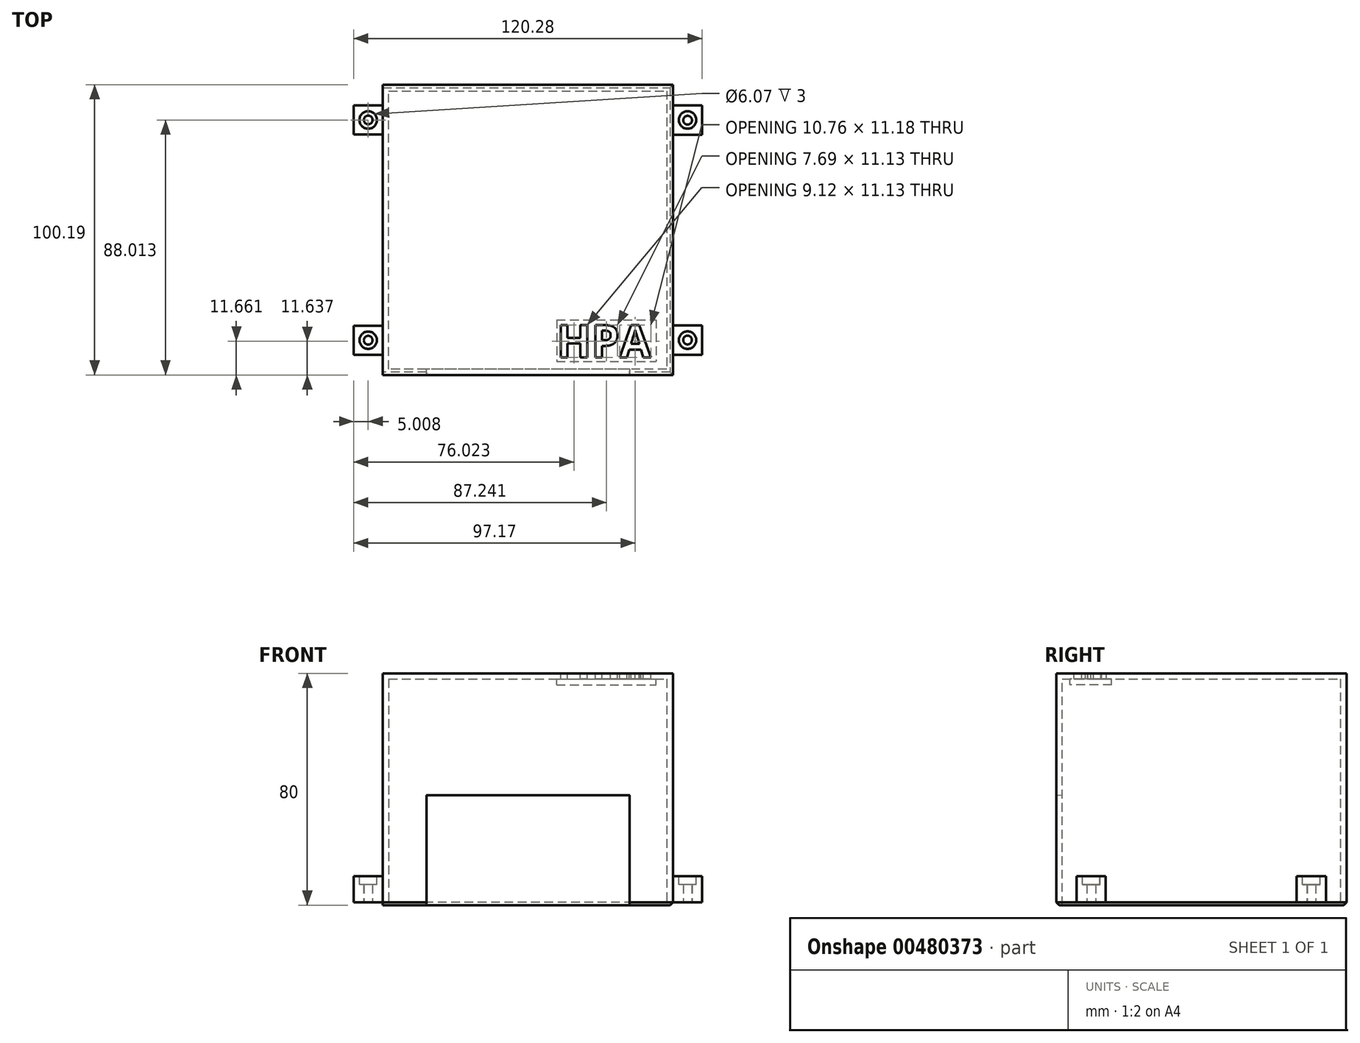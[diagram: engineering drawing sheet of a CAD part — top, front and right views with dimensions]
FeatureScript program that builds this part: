
annotation { "Feature Type Name" : "Feature", "Feature Type Description" : "" }
export const myFeature = defineFeature(function(context is Context, id is Id, definition is map)
    precondition{}
    {
        {
            var Q0;
            Q0=qCreatedBy(makeId("Right.planeOp"),FACE);
            cPlane(context, id + "F0", {"entities" : qUnion([Q0]), "cplaneType" : CPlaneType.OFFSET, "offset" : 100 * mm, "width" : 150 * mm, "height" : 150 * mm});
        }
        {
            var Q0;
            Q0=qCreatedBy(makeId("Front.planeOp"),FACE);
            cPlane(context, id + "F1", {"entities" : qUnion([Q0]), "cplaneType" : CPlaneType.OFFSET, "offset" : 100 * mm, "oppositeDirection" : true, "width" : 150 * mm, "height" : 150 * mm});
        }
        {
            var Q0;
            Q0=qCreatedBy(makeId("Top.planeOp"),FACE);
            var sketch = newSketch(context, id + "F2", { "sketchPlane" : qUnion([Q0])});
            skLineSegment(sketch, "E0.bottom", {"start": v(0, 0) * mm, "end": v(100.19, 0) * mm});
            skLineSegment(sketch, "E0.top", {"start": v(0, 100.19) * mm, "end": v(100.19, 100.19) * mm});
            skLineSegment(sketch, "E0.left", {"start": v(0, 0) * mm, "end": v(0, 100.19) * mm});
            skLineSegment(sketch, "E0.right", {"start": v(100.19, 0) * mm, "end": v(100.19, 100.19) * mm});
            skSolve(sketch);
        }
        {
            var Q0;
            Q0=qCreatedBy(id+"F1.planeOp",FACE);
            cPlane(context, id + "F3", {"entities" : qUnion([Q0]), "cplaneType" : CPlaneType.OFFSET, "offset" : 2 * mm, "width" : 150 * mm, "height" : 150 * mm});
        }
        {
            var Q0;
            Q0=qCreatedBy(makeId("Front.planeOp"),FACE);
            cPlane(context, id + "F4", {"entities" : qUnion([Q0]), "cplaneType" : CPlaneType.OFFSET, "offset" : 2 * mm, "oppositeDirection" : true, "width" : 150 * mm, "height" : 150 * mm});
        }
        {
            var Q0;
            Q0=qCreatedBy(makeId("Top.planeOp"),FACE);
            var sketch = newSketch(context, id + "F5", { "sketchPlane" : qUnion([Q0])});
            skLineSegment(sketch, "E1.bottom", {"start": v(2, 2) * mm, "end": v(97.96, 2) * mm});
            skLineSegment(sketch, "E1.top", {"start": v(2, 98.03) * mm, "end": v(97.96, 98.03) * mm});
            skLineSegment(sketch, "E1.left", {"start": v(2, 2) * mm, "end": v(2, 98.03) * mm});
            skLineSegment(sketch, "E1.right", {"start": v(97.96, 2) * mm, "end": v(97.96, 98.03) * mm});
            skSolve(sketch);
        }
        {
            var Q0;
            Q0=makeQuery(id+"F2.imprint","IMPRINT",FACE,{"disambiguationData":[TD([[makeQuery(id+"F2.imprint","IMPRINT",EDGE,{"derivedFrom":sQuery(id+"F2.wireOp",EDGE,"E0.bottom")}),1.0]])]});
            extrude(context, id + "F6", {"entities" : qUnion([Q0]), "depth" : 80 * mm, "hasDraft" : true, "draftAngle" : 0 * degree});
        }
        {
            var Q0;
            Q0 = qSketchRegion(id + "F5", true);
            extrude(context, id + "F7", {"entities" : qUnion([Q0]), "operationType" : NewBodyOperationType.REMOVE, "depth" : 78 * mm, "hasDraft" : true, "draftAngle" : 0 * degree});
        }
        {
            var Q0;
            Q0=qCreatedBy(makeId("Top.planeOp"),FACE);
            var sketch = newSketch(context, id + "F8", { "sketchPlane" : qUnion([Q0])});
            skLineSegment(sketch, "E2.bottom", {"start": v(0, 93.06) * mm, "end": v(-10.06, 93.06) * mm});
            skLineSegment(sketch, "E2.top", {"start": v(0, 82.97) * mm, "end": v(-10.06, 82.97) * mm});
            skLineSegment(sketch, "E2.left", {"start": v(0, 93.06) * mm, "end": v(0, 82.97) * mm});
            skLineSegment(sketch, "E2.right", {"start": v(-10.06, 93.06) * mm, "end": v(-10.06, 82.97) * mm});
            skSolve(sketch);
        }
        {
            var Q0;
            Q0=qCreatedBy(makeId("Top.planeOp"),FACE);
            var sketch = newSketch(context, id + "F9", { "sketchPlane" : qUnion([Q0])});
            skLineSegment(sketch, "E3.bottom", {"start": v(0, 6.97) * mm, "end": v(-10.04, 6.97) * mm});
            skLineSegment(sketch, "E3.top", {"start": v(0, 17.01) * mm, "end": v(-10.04, 17.01) * mm});
            skLineSegment(sketch, "E3.left", {"start": v(0, 6.97) * mm, "end": v(0, 17.01) * mm});
            skLineSegment(sketch, "E3.right", {"start": v(-10.04, 6.97) * mm, "end": v(-10.04, 17.01) * mm});
            skSolve(sketch);
        }
        {
            var Q0;
            Q0=qCreatedBy(makeId("Top.planeOp"),FACE);
            var sketch = newSketch(context, id + "F10", { "sketchPlane" : qUnion([Q0])});
            skLineSegment(sketch, "E4.bottom", {"start": v(100.16, 7) * mm, "end": v(110.2, 7) * mm});
            skLineSegment(sketch, "E4.top", {"start": v(100.16, 17.04) * mm, "end": v(110.2, 17.04) * mm});
            skLineSegment(sketch, "E4.left", {"start": v(100.16, 7) * mm, "end": v(100.16, 17.04) * mm});
            skLineSegment(sketch, "E4.right", {"start": v(110.2, 7) * mm, "end": v(110.2, 17.04) * mm});
            skSolve(sketch);
        }
        {
            var Q0;
            Q0=qCreatedBy(makeId("Top.planeOp"),FACE);
            var sketch = newSketch(context, id + "F11", { "sketchPlane" : qUnion([Q0])});
            skLineSegment(sketch, "E5.bottom", {"start": v(100.18, 93) * mm, "end": v(110.22, 93) * mm});
            skLineSegment(sketch, "E5.top", {"start": v(100.18, 82.95) * mm, "end": v(110.22, 82.95) * mm});
            skLineSegment(sketch, "E5.left", {"start": v(100.18, 93) * mm, "end": v(100.18, 82.95) * mm});
            skLineSegment(sketch, "E5.right", {"start": v(110.22, 93) * mm, "end": v(110.22, 82.95) * mm});
            skSolve(sketch);
        }
        {
            var Q0;
            Q0=makeQuery(id+"F6.opExtrude","CAP_FACE",FACE,{"disambiguationData":[OSD([sQuery(id+"F2.wireOp",EDGE,"E0.bottom"),sQuery(id+"F2.wireOp",EDGE,"E0.top"),sQuery(id+"F2.wireOp",EDGE,"E0.left"),sQuery(id+"F2.wireOp",EDGE,"E0.right")])],"isStart":false});
            cPlane(context, id + "F12", {"entities" : qUnion([Q0]), "cplaneType" : CPlaneType.OFFSET, "offset" : 0 * mm, "oppositeDirection" : true, "width" : 150 * mm, "height" : 150 * mm});
        }
        {
            var Q0;
            Q0=makeQuery(id+"F8.imprint","IMPRINT",FACE,{"disambiguationData":[TD([[makeQuery(id+"F8.imprint","IMPRINT",EDGE,{"derivedFrom":sQuery(id+"F8.wireOp",EDGE,"E2.bottom")}),1.0]])]});
            var Q1;
            Q1=makeQuery(id+"F11.imprint","IMPRINT",FACE,{"disambiguationData":[TD([[makeQuery(id+"F11.imprint","IMPRINT",EDGE,{"derivedFrom":sQuery(id+"F11.wireOp",EDGE,"E5.bottom")}),-1.0]])]});
            var Q2;
            Q2=makeQuery(id+"F10.imprint","IMPRINT",FACE,{"disambiguationData":[TD([[makeQuery(id+"F10.imprint","IMPRINT",EDGE,{"derivedFrom":sQuery(id+"F10.wireOp",EDGE,"E4.bottom")}),1.0]])]});
            var Q3;
            Q3=makeQuery(id+"F9.imprint","IMPRINT",FACE,{"disambiguationData":[TD([[makeQuery(id+"F9.imprint","IMPRINT",EDGE,{"derivedFrom":sQuery(id+"F9.wireOp",EDGE,"E3.bottom")}),-1.0]])]});
            extrude(context, id + "F13", {"entities" : qUnion([Q0, Q1, Q2, Q3]), "operationType" : NewBodyOperationType.ADD, "depth" : 10 * mm, "hasDraft" : true, "draftAngle" : 0 * degree});
        }
        {
            var Q0;
            Q0 = qSketchRegion(id + "F8", true);
            var Q1;
            Q1 = qSketchRegion(id + "F9", true);
            var Q2;
            Q2 = qSketchRegion(id + "F11", true);
            var Q3;
            Q3 = qSketchRegion(id + "F10", true);
            extrude(context, id + "F14", {"entities" : qUnion([Q0, Q1, Q2, Q3]), "operationType" : NewBodyOperationType.REMOVE, "depth" : 1 * mm, "hasDraft" : true, "draftAngle" : 0 * degree});
        }
        {
            var Q0;
            Q0=qCreatedBy(makeId("Top.planeOp"),FACE);
            var sketch = newSketch(context, id + "F15", { "sketchPlane" : qUnion([Q0])});
            skCircle(sketch, "E6", {"center": v(-5.05, 12) * mm, "radius": 3 * mm});
            skCircle(sketch, "E7", {"center": v(-5.05, 88.01) * mm, "radius": 3.03 * mm});
            skCircle(sketch, "E8", {"center": v(105.2, 88.01) * mm, "radius": 3.02 * mm});
            skCircle(sketch, "E9", {"center": v(105.2, 12.02) * mm, "radius": 3 * mm});
            skSolve(sketch);
        }
        {
            var Q0;
            Q0 = qSketchRegion(id + "F15", true);
            extrude(context, id + "F16", {"entities" : qUnion([Q0]), "operationType" : NewBodyOperationType.REMOVE, "depth" : 25 * mm, "hasDraft" : true, "draftAngle" : 0 * degree});
        }
        {
            var Q0;
            Q0 = qSketchRegion(id + "F15", true);
            extrude(context, id + "F17", {"entities" : qUnion([Q0]), "operationType" : NewBodyOperationType.ADD, "depth" : 7 * mm, "hasDraft" : true, "draftAngle" : 0 * degree});
        }
        {
            var Q0;
            Q0 = qSketchRegion(id + "F15", true);
            extrude(context, id + "F18", {"entities" : qUnion([Q0]), "operationType" : NewBodyOperationType.REMOVE, "depth" : 1 * mm, "hasDraft" : true, "draftAngle" : 0 * degree});
        }
        {
            var Q0;
            Q0=qCreatedBy(makeId("Top.planeOp"),FACE);
            var sketch = newSketch(context, id + "F19", { "sketchPlane" : qUnion([Q0])});
            skCircle(sketch, "E10", {"center": v(-5.05, 12) * mm, "radius": 1.52 * mm});
            skCircle(sketch, "E11", {"center": v(105.17, 12.04) * mm, "radius": 1.5 * mm});
            skCircle(sketch, "E12", {"center": v(105.22, 87.94) * mm, "radius": 1.5 * mm});
            skCircle(sketch, "E13", {"center": v(-5.04, 88.03) * mm, "radius": 1.51 * mm});
            skSolve(sketch);
        }
        {
            var Q0;
            Q0 = qSketchRegion(id + "F19", true);
            extrude(context, id + "F20", {"entities" : qUnion([Q0]), "operationType" : NewBodyOperationType.REMOVE, "depth" : 25 * mm});
        }
        {
            var Q0;
            Q0=qCreatedBy(makeId("Front.planeOp"),FACE);
            var sketch = newSketch(context, id + "F21", { "sketchPlane" : qUnion([Q0])});
            skLineSegment(sketch, "E14.bottom", {"start": v(15.03, 37.98) * mm, "end": v(85.18, 37.98) * mm});
            skLineSegment(sketch, "E14.top", {"start": v(15.03, -2.64) * mm, "end": v(85.18, -2.64) * mm});
            skLineSegment(sketch, "E14.left", {"start": v(15.03, 37.98) * mm, "end": v(15.03, -2.64) * mm});
            skLineSegment(sketch, "E14.right", {"start": v(85.18, 37.98) * mm, "end": v(85.18, -2.64) * mm});
            skSolve(sketch);
        }
        {
            var Q0;
            Q0 = qSketchRegion(id + "F21", true);
            extrude(context, id + "F22", {"entities" : qUnion([Q0]), "operationType" : NewBodyOperationType.REMOVE, "depth" : 25 * mm, "hasSecondDirection" : true, "secondDirectionOppositeDirection" : true, "secondDirectionDepth" : 25 * mm, "hasSecondDirectionDraft" : true, "secondDirectionDraftAngle" : 3 * degree});
        }
        {
            var Q0;
            Q0=qCreatedBy(id+"F12.planeOp",FACE);
            var sketch = newSketch(context, id + "F23", { "sketchPlane" : qUnion([Q0])});
            skText(sketch, "E15", { "text": "HPA", "fontName": "OpenSans-Bold.ttf"});
            const initialGuessF23  = {"E15": [0.06, 0.00607, 1, 0, 0.01123]};
            skSetInitialGuess(sketch, initialGuessF23);
            skSolve(sketch);
        }
        {
            var Q0;
            Q0=makeQuery(id+"F6.opExtrude","CAP_EDGE",EDGE,{"disambiguationData":[OSD([sQuery(id+"F2.wireOp",EDGE,"E0.top")])],"isStart":true});
            var Q1;
            Q1=makeQuery(id+"F7.boolean.opBoolean","COPY",EDGE,{"derivedFrom":makeQuery(id+"F7.opExtrude","CAP_EDGE",EDGE,{"disambiguationData":[OSD([sQuery(id+"F5.wireOp",EDGE,"E1.top")])],"isStart":true})});
            var Q2;
            {var subQ0=sQuery(id+"F9.wireOp",EDGE,"E3.left");var subQ1=sQuery(id+"F8.wireOp",EDGE,"E2.left");var subQ2=sQuery(id+"F8.wireOp",EDGE,"E2.top");var subQ3=sQuery(id+"F2.wireOp",EDGE,"E0.left");var subQ7=sQuery(id+"F2.wireOp",EDGE,"E0.top");var subQ8=sQuery(id+"F2.wireOp",EDGE,"E0.bottom");var subQ15=makeQuery(id+"F6.opExtrude","CAP_EDGE",EDGE,{"disambiguationData":[OSD([subQ3])],"isStart":true});Q2=makeQuery(id+"F14.boolean.opBoolean","MERGE",EDGE,{"derivedFrom":[makeQuery(id+"F13.boolean.opBoolean","SPLIT",EDGE,{"disambiguationData":[TD([makeQuery(id+"F6.opExtrude","SWEPT_FACE",FACE,{"disambiguationData":[OSD([subQ8])]})])],"derivedFrom":subQ15}),makeQuery(id+"F13.boolean.opBoolean","SPLIT",EDGE,{"disambiguationData":[TD([makeQuery(id+"F6.opExtrude","SWEPT_FACE",FACE,{"disambiguationData":[OSD([subQ7])]})])],"derivedFrom":subQ15}),makeQuery(id+"F13.boolean.opBoolean","SPLIT",EDGE,{"disambiguationData":[TD([makeQuery(id+"F13.opExtrude","SWEPT_FACE",FACE,{"disambiguationData":[OSD([subQ2])]})])],"derivedFrom":subQ15}),makeQuery(id+"F14.opExtrude","CAP_EDGE",EDGE,{"disambiguationData":[OSD([subQ1])],"isStart":true}),makeQuery(id+"F14.opExtrude","CAP_EDGE",EDGE,{"disambiguationData":[OSD([subQ0])],"isStart":true})]});}
            var Q3;
            Q3=makeQuery(id+"F7.boolean.opBoolean","COPY",EDGE,{"derivedFrom":makeQuery(id+"F7.opExtrude","CAP_EDGE",EDGE,{"disambiguationData":[OSD([sQuery(id+"F5.wireOp",EDGE,"E1.left")])],"isStart":true})});
            var Q4;
            {var subQ0=sQuery(id+"F5.wireOp",EDGE,"E1.bottom");Q4=makeQuery(id+"F22.boolean.opBoolean","SPLIT",EDGE,{"disambiguationData":[TD([makeQuery(id+"F7.boolean.opBoolean","COPY",FACE,{"derivedFrom":makeQuery(id+"F7.opExtrude","SWEPT_FACE",FACE,{"disambiguationData":[OSD([sQuery(id+"F5.wireOp",EDGE,"E1.left")])]})})])],"derivedFrom":makeQuery(id+"F7.boolean.opBoolean","COPY",EDGE,{"derivedFrom":makeQuery(id+"F7.opExtrude","CAP_EDGE",EDGE,{"disambiguationData":[OSD([subQ0])],"isStart":true})})});}
            var Q5;
            {var subQ0=sQuery(id+"F2.wireOp",EDGE,"E0.left");var subQ2=sQuery(id+"F2.wireOp",EDGE,"E0.bottom");Q5=makeQuery(id+"F22.boolean.opBoolean","SPLIT",EDGE,{"disambiguationData":[TD([makeQuery(id+"F6.opExtrude","SWEPT_FACE",FACE,{"disambiguationData":[OSD([subQ0])]})])],"derivedFrom":makeQuery(id+"F6.opExtrude","CAP_EDGE",EDGE,{"disambiguationData":[OSD([subQ2])],"isStart":true})});}
            var Q6;
            {var subQ0=sQuery(id+"F5.wireOp",EDGE,"E1.bottom");Q6=makeQuery(id+"F22.boolean.opBoolean","SPLIT",EDGE,{"disambiguationData":[TD([makeQuery(id+"F7.boolean.opBoolean","COPY",FACE,{"derivedFrom":makeQuery(id+"F7.opExtrude","SWEPT_FACE",FACE,{"disambiguationData":[OSD([sQuery(id+"F5.wireOp",EDGE,"E1.right")])]})})])],"derivedFrom":makeQuery(id+"F7.boolean.opBoolean","COPY",EDGE,{"derivedFrom":makeQuery(id+"F7.opExtrude","CAP_EDGE",EDGE,{"disambiguationData":[OSD([subQ0])],"isStart":true})})});}
            var Q7;
            {var subQ0=sQuery(id+"F2.wireOp",EDGE,"E0.right");var subQ1=sQuery(id+"F2.wireOp",EDGE,"E0.bottom");Q7=makeQuery(id+"F22.boolean.opBoolean","SPLIT",EDGE,{"disambiguationData":[TD([makeQuery(id+"F6.opExtrude","SWEPT_FACE",FACE,{"disambiguationData":[OSD([subQ0])]})])],"derivedFrom":makeQuery(id+"F6.opExtrude","CAP_EDGE",EDGE,{"disambiguationData":[OSD([subQ1])],"isStart":true})});}
            var Q8;
            {var subQ0=sQuery(id+"F2.wireOp",EDGE,"E0.right");var subQ1=sQuery(id+"F10.wireOp",EDGE,"E4.top");Q8=makeQuery(id+"F13.boolean.opBoolean","SPLIT",EDGE,{"disambiguationData":[TD([makeQuery(id+"F13.opExtrude","SWEPT_FACE",FACE,{"disambiguationData":[OSD([subQ1])]})])],"derivedFrom":makeQuery(id+"F6.opExtrude","CAP_EDGE",EDGE,{"disambiguationData":[OSD([subQ0])],"isStart":true})});}
            var Q9;
            Q9=makeQuery(id+"F7.boolean.opBoolean","COPY",EDGE,{"derivedFrom":makeQuery(id+"F7.opExtrude","CAP_EDGE",EDGE,{"disambiguationData":[OSD([sQuery(id+"F5.wireOp",EDGE,"E1.right")])],"isStart":true})});
            chamfer(context, id + "F24", {"entities" : qUnion([Q0, Q1, Q2, Q3, Q4, Q5, Q6, Q7, Q8, Q9]), "width" : 1 * mm, "tangentPropagation" : true});
        }
        {
            var Q0;
            Q0=qCreatedBy(makeId("Right.planeOp"),FACE);
            var sketch = newSketch(context, id + "F25", { "sketchPlane" : qUnion([Q0])});
            skLineSegment(sketch, "E16.bottom", {"start": v(16.75, 9.72) * mm, "end": v(7.24, 9.72) * mm});
            skLineSegment(sketch, "E16.top", {"start": v(16.75, 1.23) * mm, "end": v(7.24, 1.23) * mm});
            skLineSegment(sketch, "E16.left", {"start": v(16.75, 9.72) * mm, "end": v(16.75, 1.23) * mm});
            skLineSegment(sketch, "E16.right", {"start": v(7.24, 9.72) * mm, "end": v(7.24, 1.23) * mm});
            skLineSegment(sketch, "E17.bottom", {"start": v(92.84, 9.8) * mm, "end": v(83.16, 9.8) * mm});
            skLineSegment(sketch, "E17.top", {"start": v(92.84, 1.24) * mm, "end": v(83.16, 1.24) * mm});
            skLineSegment(sketch, "E17.left", {"start": v(92.84, 9.8) * mm, "end": v(92.84, 1.24) * mm});
            skLineSegment(sketch, "E17.right", {"start": v(83.16, 9.8) * mm, "end": v(83.16, 1.24) * mm});
            skSolve(sketch);
        }
        {
            var Q0;
            Q0 = qSketchRegion(id + "F25", true);
            extrude(context, id + "F26", {"entities" : qUnion([Q0]), "operationType" : NewBodyOperationType.ADD, "depth" : 1 * mm, "hasSecondDirection" : true, "secondDirectionOppositeDirection" : true, "secondDirectionDepth" : 1 * mm});
        }
        {
            var Q0;
            Q0=makeQuery(id+"F6.opExtrude","SWEPT_FACE",FACE,{"disambiguationData":[OSD([sQuery(id+"F2.wireOp",EDGE,"E0.right")])]});
            cPlane(context, id + "F27", {"entities" : qUnion([Q0]), "cplaneType" : CPlaneType.OFFSET, "offset" : 0 * mm, "width" : 150 * mm, "height" : 150 * mm});
        }
        {
            var Q0;
            Q0=qCreatedBy(id+"F27.planeOp",FACE);
            var sketch = newSketch(context, id + "F28", { "sketchPlane" : qUnion([Q0])});
            skLineSegment(sketch, "E18.bottom", {"start": v(7.54, 9.6) * mm, "end": v(16.47, 9.6) * mm});
            skLineSegment(sketch, "E18.top", {"start": v(7.54, 1.44) * mm, "end": v(16.47, 1.44) * mm});
            skLineSegment(sketch, "E18.left", {"start": v(7.54, 9.6) * mm, "end": v(7.54, 1.44) * mm});
            skLineSegment(sketch, "E18.right", {"start": v(16.47, 9.6) * mm, "end": v(16.47, 1.44) * mm});
            skLineSegment(sketch, "E19.bottom", {"start": v(83.33, 9.7) * mm, "end": v(92.62, 9.7) * mm});
            skLineSegment(sketch, "E19.top", {"start": v(83.33, 1.44) * mm, "end": v(92.62, 1.44) * mm});
            skLineSegment(sketch, "E19.left", {"start": v(83.33, 9.7) * mm, "end": v(83.33, 1.44) * mm});
            skLineSegment(sketch, "E19.right", {"start": v(92.62, 9.7) * mm, "end": v(92.62, 1.44) * mm});
            skSolve(sketch);
        }
        {
            var Q0;
            Q0 = qSketchRegion(id + "F28", true);
            extrude(context, id + "F29", {"entities" : qUnion([Q0]), "operationType" : NewBodyOperationType.ADD, "depth" : 1 * mm, "hasSecondDirection" : true, "secondDirectionOppositeDirection" : true, "secondDirectionDepth" : 1 * mm});
        }
        {
            var Q0;
            Q0 = qSketchRegion(id + "F23", true);
            extrude(context, id + "F30", {"entities" : qUnion([Q0]), "operationType" : NewBodyOperationType.REMOVE, "oppositeDirection" : true, "depth" : 10 * mm});
        }
        {
            var Q0;
            Q0=qCreatedBy(id+"F12.planeOp",FACE);
            cPlane(context, id + "F31", {"entities" : qUnion([Q0]), "cplaneType" : CPlaneType.OFFSET, "offset" : 2 * mm, "oppositeDirection" : true, "width" : 150 * mm, "height" : 150 * mm});
        }
        {
            var Q0;
            Q0=qCreatedBy(id+"F31.planeOp",FACE);
            var sketch = newSketch(context, id + "F32", { "sketchPlane" : qUnion([Q0])});
            skLineSegment(sketch, "E20.bottom", {"start": v(60.01, 19.04) * mm, "end": v(94.37, 19.04) * mm});
            skLineSegment(sketch, "E20.top", {"start": v(60.01, 4.67) * mm, "end": v(94.37, 4.67) * mm});
            skLineSegment(sketch, "E20.left", {"start": v(60.01, 19.04) * mm, "end": v(60.01, 4.67) * mm});
            skLineSegment(sketch, "E20.right", {"start": v(94.37, 19.04) * mm, "end": v(94.37, 4.67) * mm});
            skSolve(sketch);
        }
        {
            var Q0;
            Q0 = qSketchRegion(id + "F32", true);
            extrude(context, id + "F33", {"entities" : qUnion([Q0]), "oppositeDirection" : true, "depth" : 2 * mm});
        }
    });
